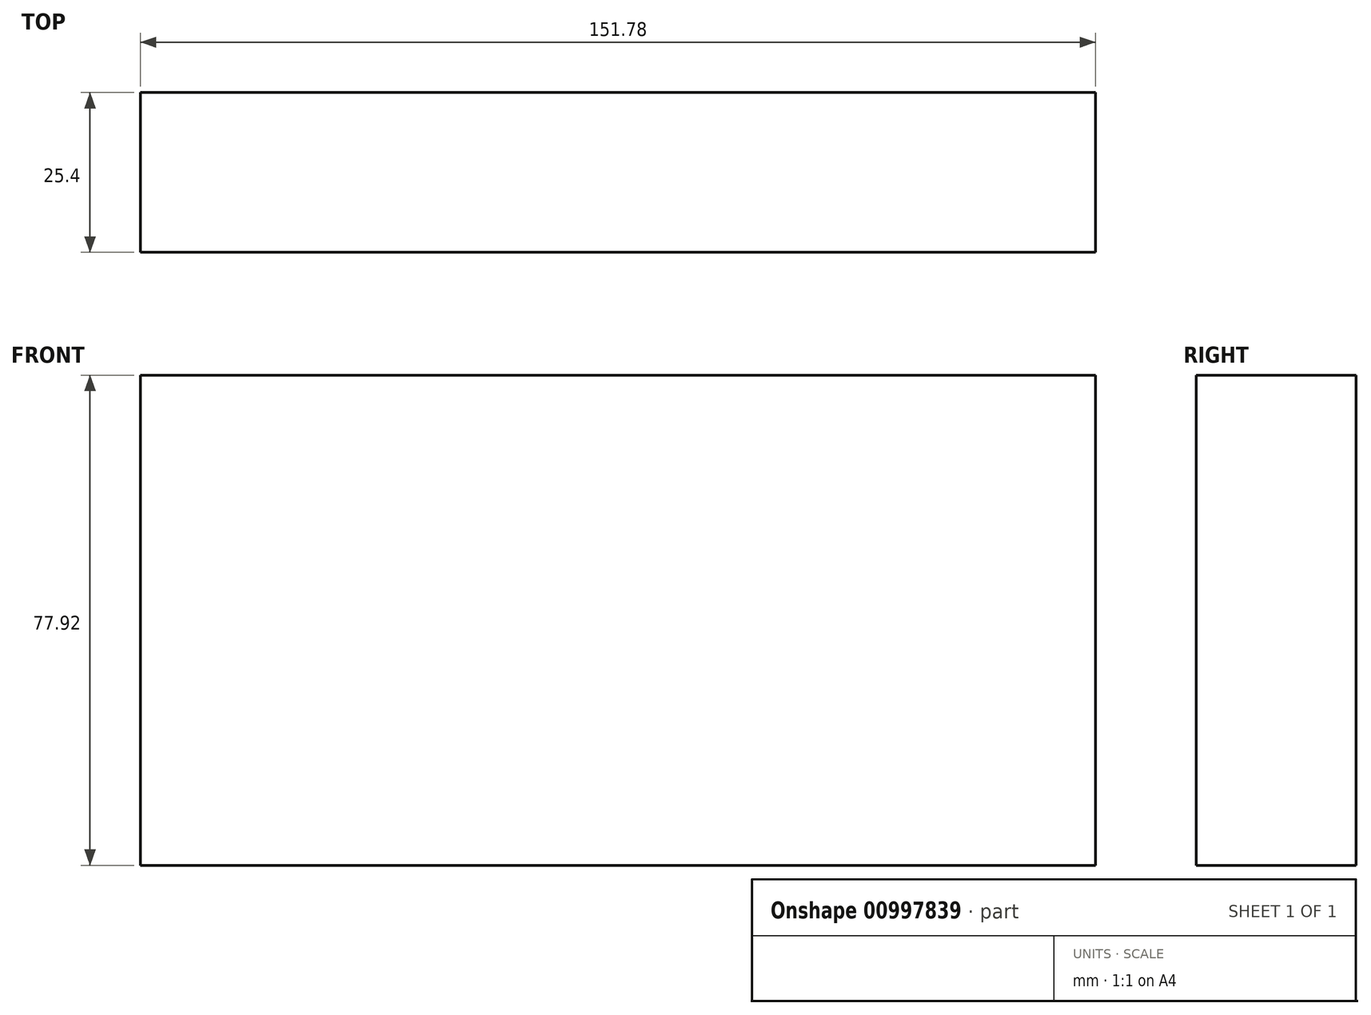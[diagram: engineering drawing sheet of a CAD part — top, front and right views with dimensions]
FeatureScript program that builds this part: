
annotation { "Feature Type Name" : "Feature", "Feature Type Description" : "" }
export const myFeature = defineFeature(function(context is Context, id is Id, definition is map)
    precondition{}
    {
        {
            var Q0;
            Q0=qCreatedBy(makeId("Front.planeOp"),FACE);
            var sketch = newSketch(context, id + "F0", { "sketchPlane" : qUnion([Q0])});
            skLineSegment(sketch, "E0", {"start": v(-75.89, -38.96) * mm, "end": v(0, -38.96) * mm});
            skLineSegment(sketch, "E1.MirrorCS", {"start": v(-75.89, 38.96) * mm, "end": v(0, 38.96) * mm});
            skLineSegment(sketch, "E2.MirrorCS", {"start": v(75.89, 38.96) * mm, "end": v(0, 38.96) * mm});
            skLineSegment(sketch, "E3.MirrorCS", {"start": v(75.89, -38.96) * mm, "end": v(0, -38.96) * mm});
            skLineSegment(sketch, "E4", {"start": v(0, 38.96) * mm, "end": v(0, -38.96) * mm});
            skLineSegment(sketch, "E5", {"start": v(-75.89, 38.96) * mm, "end": v(-75.89, -38.96) * mm});
            skLineSegment(sketch, "E6", {"start": v(75.89, 38.96) * mm, "end": v(75.89, -38.96) * mm});
            skSolve(sketch);
        }
        {
            var Q0;
            Q0=makeQuery(id+"F0.imprint","IMPRINT",FACE,{"disambiguationData":[TD([[makeQuery(id+"F0.imprint","IMPRINT",EDGE,{"derivedFrom":sQuery(id+"F0.wireOp",EDGE,"E2.MirrorCS")}),1.0]])]});
            var Q1;
            Q1=makeQuery(id+"F0.imprint","IMPRINT",FACE,{"disambiguationData":[TD([[makeQuery(id+"F0.imprint","IMPRINT",EDGE,{"derivedFrom":sQuery(id+"F0.wireOp",EDGE,"E0")}),1.0]])]});
            extrude(context, id + "F1", {"entities" : qUnion([Q0, Q1]), "endBound" : BoundingType.SYMMETRIC, "depth" : 25.4 * mm, "offsetDistance" : 25.4 * mm});
        }
        {
            var Q0;
            Q0=makeQuery(id+"F1.opExtrude","CAP_FACE",FACE,{"disambiguationData":[OSD([sQuery(id+"F0.wireOp",EDGE,"E0"),sQuery(id+"F0.wireOp",EDGE,"E1.MirrorCS"),sQuery(id+"F0.wireOp",EDGE,"E2.MirrorCS"),sQuery(id+"F0.wireOp",EDGE,"E3.MirrorCS"),sQuery(id+"F0.wireOp",EDGE,"E5"),sQuery(id+"F0.wireOp",EDGE,"E6")])],"isStart":false});
            shell(context, id + "F2", {"entities" : qUnion([Q0]), "thickness" : 25.4 * mm});
        }
    });
